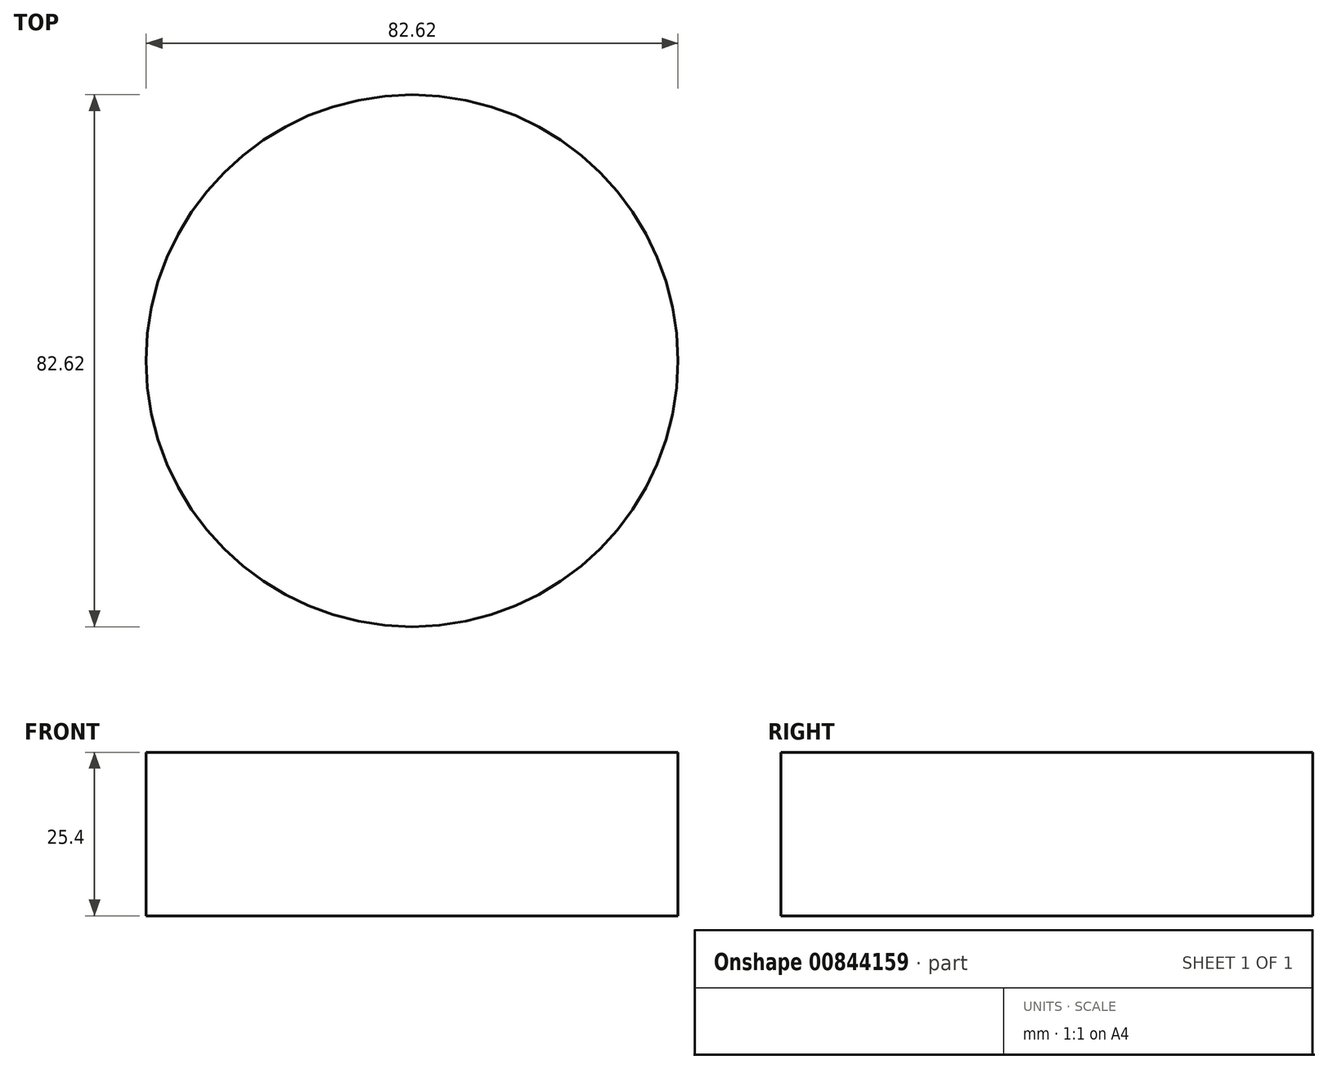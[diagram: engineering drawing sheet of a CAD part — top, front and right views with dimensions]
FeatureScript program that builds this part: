
annotation { "Feature Type Name" : "Feature", "Feature Type Description" : "" }
export const myFeature = defineFeature(function(context is Context, id is Id, definition is map)
    precondition{}
    {
        {
            var Q0;
            Q0=qCreatedBy(makeId("Top.planeOp"),FACE);
            var sketch = newSketch(context, id + "F0", { "sketchPlane" : qUnion([Q0])});
            skCircle(sketch, "E0", {"center": v(0, 0) * mm, "radius": 41.31 * mm});
            skSolve(sketch);
        }
        {
            var Q0;
            Q0=makeQuery(id+"F0.imprint","IMPRINT",FACE,{"disambiguationData":[TD([[makeQuery(id+"F0.imprint","IMPRINT",EDGE,{"derivedFrom":sQuery(id+"F0.wireOp",EDGE,"E0")}),1.0]])]});
            extrude(context, id + "F1", {"entities" : qUnion([Q0]), "depth" : 25.4 * mm, "offsetDistance" : 25.4 * mm});
        }
    });
